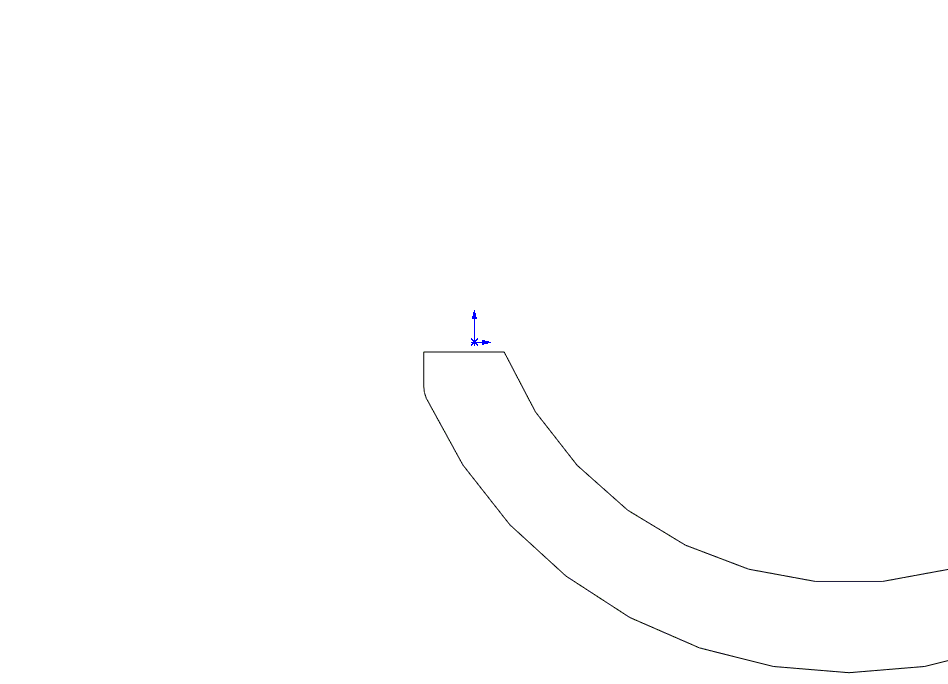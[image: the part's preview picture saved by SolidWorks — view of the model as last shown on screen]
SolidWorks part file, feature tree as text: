
SOLIDWORKS PART (.sldprt)
format: sldprt  version: not decoded by parser v0  size: 195,584 bytes
history: native  units: mm
features: sketch x3, extrude x3, fillet x2, material x1, plane x1, mirror x1 (+13 scaffold rows collapsed)
feature tree (24):
  scaffold x13  (default folders/planes/origin — collapsed)
  material  "Material <not specified>"
  sketch  "Sketch1"  dims[c1.D5=152.4mm c1.D1=25.4mm c1.D2=25.4mm c1.D3=3.175mm c2.D2=25.4mm c2.D4=25.4mm c2.D1=12.7mm c3.D2=38.1mm c3.D4=3.175mm c4.D2=31.75mm c4.D3=12.7mm c4.D4=38.1mm]
  extrude  "Extrude1"  Depth=6.35mm
  sketch  "Sketch2"  dims[c1.D1=12.7mm c1.D2=114.3mm c1.D3=12.7mm c2.D2=3.175mm c2.D5=6.35mm c2.D4=0.0mm]
  extrude  "Extrude2"  [1 undecoded]
  sketch  "Sketch3"  dims[D1=25.4mm D2=9.525mm D3=0.0mm]
  extrude  "Extrude3"  [1 undecoded]
  fillet  "Fillet1"  Radius=9.525mm
  fillet  "Fillet2"  Radius=3.175mm
  plane  "Plane1"
  mirror  "Mirror1"
decode coverage: 6 of 9 modeling features carry decoded parameters
note: 2 parameter values undecoded
note: suppression state not decoded; provenance and decode notes live in map.json
